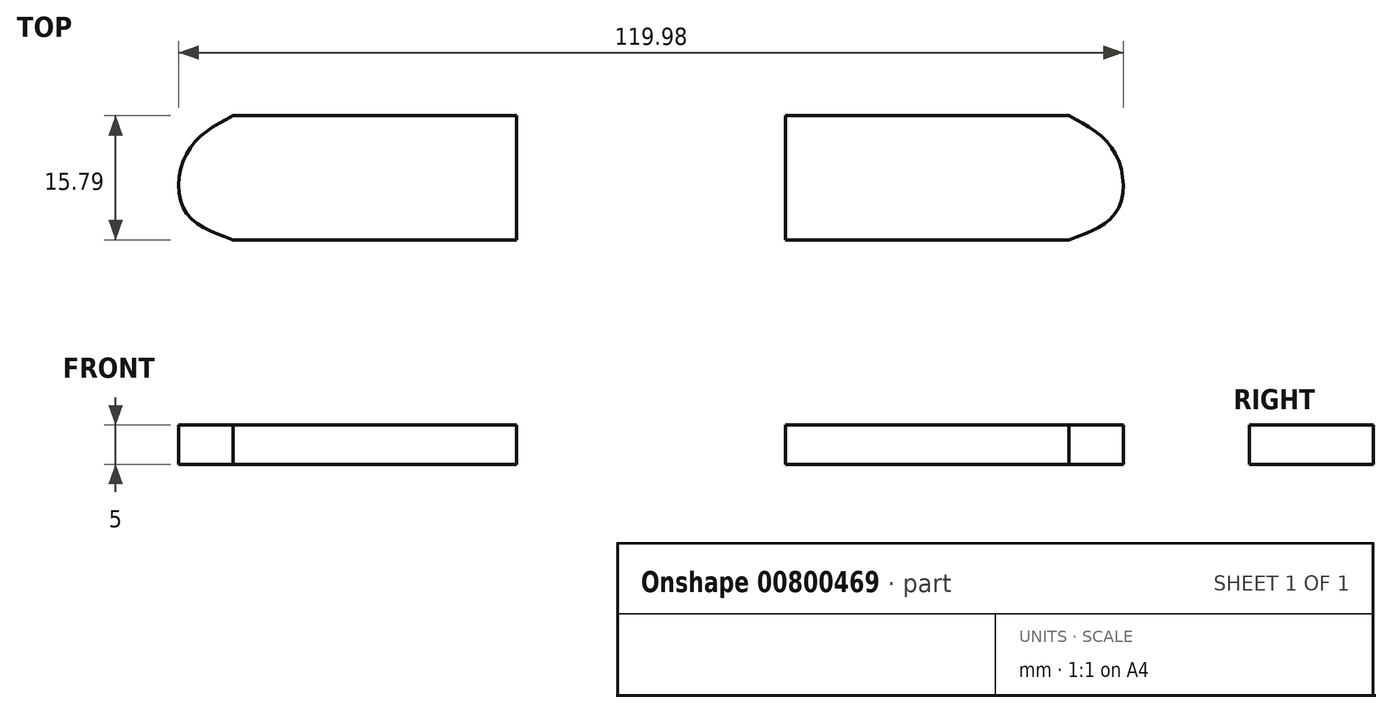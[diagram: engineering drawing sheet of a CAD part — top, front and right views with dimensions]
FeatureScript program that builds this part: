
annotation { "Feature Type Name" : "Feature", "Feature Type Description" : "" }
export const myFeature = defineFeature(function(context is Context, id is Id, definition is map)
    precondition{}
    {
        {
            var Q0;
            Q0=qCreatedBy(makeId("Top.planeOp"),FACE);
            var sketch = newSketch(context, id + "F0", { "sketchPlane" : qUnion([Q0])});
            skLineSegment(sketch, "E0", {"start": v(-17.09, 18.89) * mm, "end": v(-53.07, 18.89) * mm});
            skFitSpline(sketch, "E1", {"points": [v(-53.07, 18.89) * mm, v(-58.86, 14.3) * mm, v(-59.26, 6.9) * mm, v(-53.07, 3.1) * mm], "startDerivative": vector(-20.31, -10.81) * mm, "endDerivative": vector(22.91, -8.08) * mm});
            skLineSegment(sketch, "E2", {"start": v(-53.07, 3.1) * mm, "end": v(-17.09, 3.1) * mm});
            skLineSegment(sketch, "E3", {"start": v(-17.09, 3.1) * mm, "end": v(-17.09, 18.89) * mm});
            skSolve(sketch);
        }
        {
            var Q0;
            Q0 = qSketchRegion(id + "F0", true);
            extrude(context, id + "F1", {"entities" : qUnion([Q0]), "depth" : 5 * mm, "offsetDistance" : 25 * mm});
        }
        {
            var Q0;
            Q0=makeQuery(id+"F1.opExtrude","SWEPT_BODY",BODY,{"disambiguationData":[OSD([sQuery(id+"F0.wireOp",EDGE,"E0"),sQuery(id+"F0.wireOp",EDGE,"E1"),sQuery(id+"F0.wireOp",EDGE,"E2"),sQuery(id+"F0.wireOp",EDGE,"E3")])]});
            var Q1;
            Q1=qCreatedBy(makeId("Right.planeOp"),FACE);
            mirror(context, id + "F2", {"entities" : qUnion([Q0]), "mirrorPlane" : qUnion([Q1])});
        }
    });
